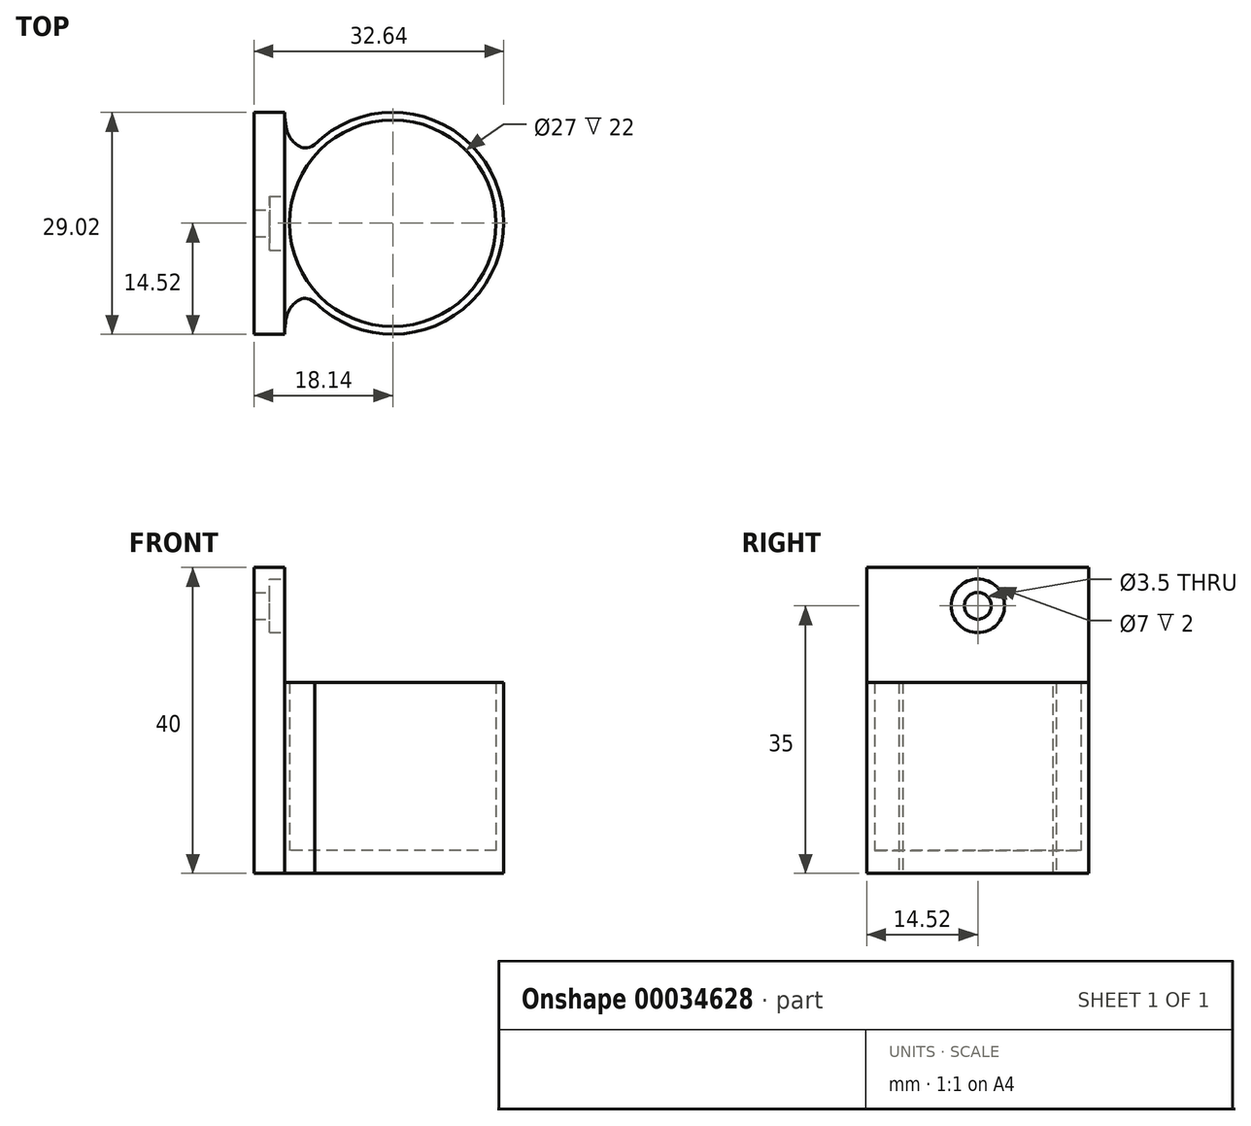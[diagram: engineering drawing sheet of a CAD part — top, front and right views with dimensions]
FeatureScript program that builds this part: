
annotation { "Feature Type Name" : "Feature", "Feature Type Description" : "" }
export const myFeature = defineFeature(function(context is Context, id is Id, definition is map)
    precondition{}
    {
        {
            var Q0;
            Q0=qCreatedBy(makeId("Top.planeOp"),FACE);
            var sketch = newSketch(context, id + "F0", { "sketchPlane" : qUnion([Q0])});
            skCircle(sketch, "E0", {"center": v(0, 0) * mm, "radius": 14.5 * mm});
            skCircle(sketch, "E1", {"center": v(0, 0) * mm, "radius": 13.5 * mm});
            skLineSegment(sketch, "E2.bottom", {"start": v(-18.14, 14.48) * mm, "end": v(-14.14, 14.48) * mm});
            skLineSegment(sketch, "E2.top", {"start": v(-18.14, -14.52) * mm, "end": v(-14.14, -14.52) * mm});
            skLineSegment(sketch, "E2.left", {"start": v(-18.14, 14.48) * mm, "end": v(-18.14, -14.52) * mm});
            skLineSegment(sketch, "E2.right", {"start": v(-14.14, 14.48) * mm, "end": v(-14.14, -14.52) * mm});
            skLineSegment(sketch, "E3", {"start": v(0, 14.5) * mm, "end": v(-42.27, 14.5) * mm, "construction": true});
            skFitSpline(sketch, "E4", {"points": [v(-14.14, 14.48) * mm, v(-12.81, 10.5) * mm, v(-10.27, 10.23) * mm], "startDerivative": vector(0.37, -12.73) * mm, "endDerivative": vector(7.7, 5.07) * mm});
            skFitSpline(sketch, "E5", {"points": [v(-14.14, -14.52) * mm, v(-12.81, -10.45) * mm, v(-10.17, -10.34) * mm], "startDerivative": vector(0.18, 13.7) * mm, "endDerivative": vector(8.1, -6.23) * mm});
            skSolve(sketch);
        }
        {
            var Q0;
            {var subQ0=sQuery(id+"F0.wireOp",EDGE,"E2.right");var subQ1=sQuery(id+"F0.wireOp",EDGE,"E0");var subQ3=makeQuery(id+"F0.imprint","INTERSECT",VERTEX,{"disambiguationData":[OD(0.0)],"derivedFrom":[subQ1,subQ0]});Q0=makeQuery(id+"F0.imprint","IMPRINT",FACE,{"disambiguationData":[TD([[makeQuery(id+"F0.imprint","IMPRINT",EDGE,{"disambiguationData":[TD([[subQ3,-1.0]])],"derivedFrom":subQ1}),1.0]])]});}
            var Q1;
            {var subQ5=sQuery(id+"F0.wireOp",EDGE,"E2.bottom");Q1=makeQuery(id+"F0.imprint","IMPRINT",FACE,{"disambiguationData":[TD([[makeQuery(id+"F0.imprint","IMPRINT",EDGE,{"derivedFrom":subQ5}),-1.0]])]});}
            extrude(context, id + "F1", {"entities" : qUnion([Q0, Q1]), "depth" : 40 * mm});
        }
        {
            var Q0;
            Q0=makeQuery(id+"F0.imprint","IMPRINT",FACE,{"disambiguationData":[TD([[makeQuery(id+"F0.imprint","IMPRINT",EDGE,{"derivedFrom":sQuery(id+"F0.wireOp",EDGE,"E1")}),1.0]])]});
            extrude(context, id + "F2", {"entities" : qUnion([Q0]), "operationType" : NewBodyOperationType.ADD, "depth" : 3 * mm});
        }
        {
            var Q0;
            {var subQ0=sQuery(id+"F0.wireOp",EDGE,"E4");Q0=makeQuery(id+"F0.imprint","IMPRINT",FACE,{"disambiguationData":[TD([[makeQuery(id+"F0.imprint","IMPRINT",EDGE,{"derivedFrom":subQ0}),-1.0]])]});}
            var Q1;
            Q1=makeQuery(id+"F0.imprint","IMPRINT",FACE,{"disambiguationData":[TD([[makeQuery(id+"F0.imprint","IMPRINT",EDGE,{"derivedFrom":sQuery(id+"F0.wireOp",EDGE,"E1")}),-1.0]])]});
            var Q2;
            {var subQ0=sQuery(id+"F0.wireOp",EDGE,"E5");Q2=makeQuery(id+"F0.imprint","IMPRINT",FACE,{"disambiguationData":[TD([[makeQuery(id+"F0.imprint","IMPRINT",EDGE,{"derivedFrom":subQ0}),1.0]])]});}
            extrude(context, id + "F3", {"entities" : qUnion([Q0, Q1, Q2]), "operationType" : NewBodyOperationType.ADD, "depth" : 25 * mm});
        }
        {
            var Q0;
            Q0=makeQuery(id+"F1.opExtrude","SWEPT_FACE",FACE,{"disambiguationData":[OSD([sQuery(id+"F0.wireOp",EDGE,"E2.right")])]});
            var sketch = newSketch(context, id + "F4", { "sketchPlane" : qUnion([Q0])});
            skCircle(sketch, "E6", {"center": v(0, 35) * mm, "radius": 3.5 * mm});
            skCircle(sketch, "E7", {"center": v(0, 35) * mm, "radius": 1.75 * mm});
            skSolve(sketch);
        }
        {
            var Q0;
            Q0=makeQuery(id+"F4.imprint","IMPRINT",FACE,{"disambiguationData":[TD([[makeQuery(id+"F4.imprint","IMPRINT",EDGE,{"derivedFrom":sQuery(id+"F4.wireOp",EDGE,"E7")}),1.0]])]});
            extrude(context, id + "F5", {"entities" : qUnion([Q0]), "operationType" : NewBodyOperationType.REMOVE, "oppositeDirection" : true, "depth" : 25 * mm});
        }
        {
            var Q0;
            Q0=makeQuery(id+"F4.imprint","IMPRINT",FACE,{"disambiguationData":[TD([[makeQuery(id+"F4.imprint","IMPRINT",EDGE,{"derivedFrom":sQuery(id+"F4.wireOp",EDGE,"E6")}),1.0]])]});
            extrude(context, id + "F6", {"entities" : qUnion([Q0]), "operationType" : NewBodyOperationType.REMOVE, "oppositeDirection" : true, "depth" : 2 * mm});
        }
    });
